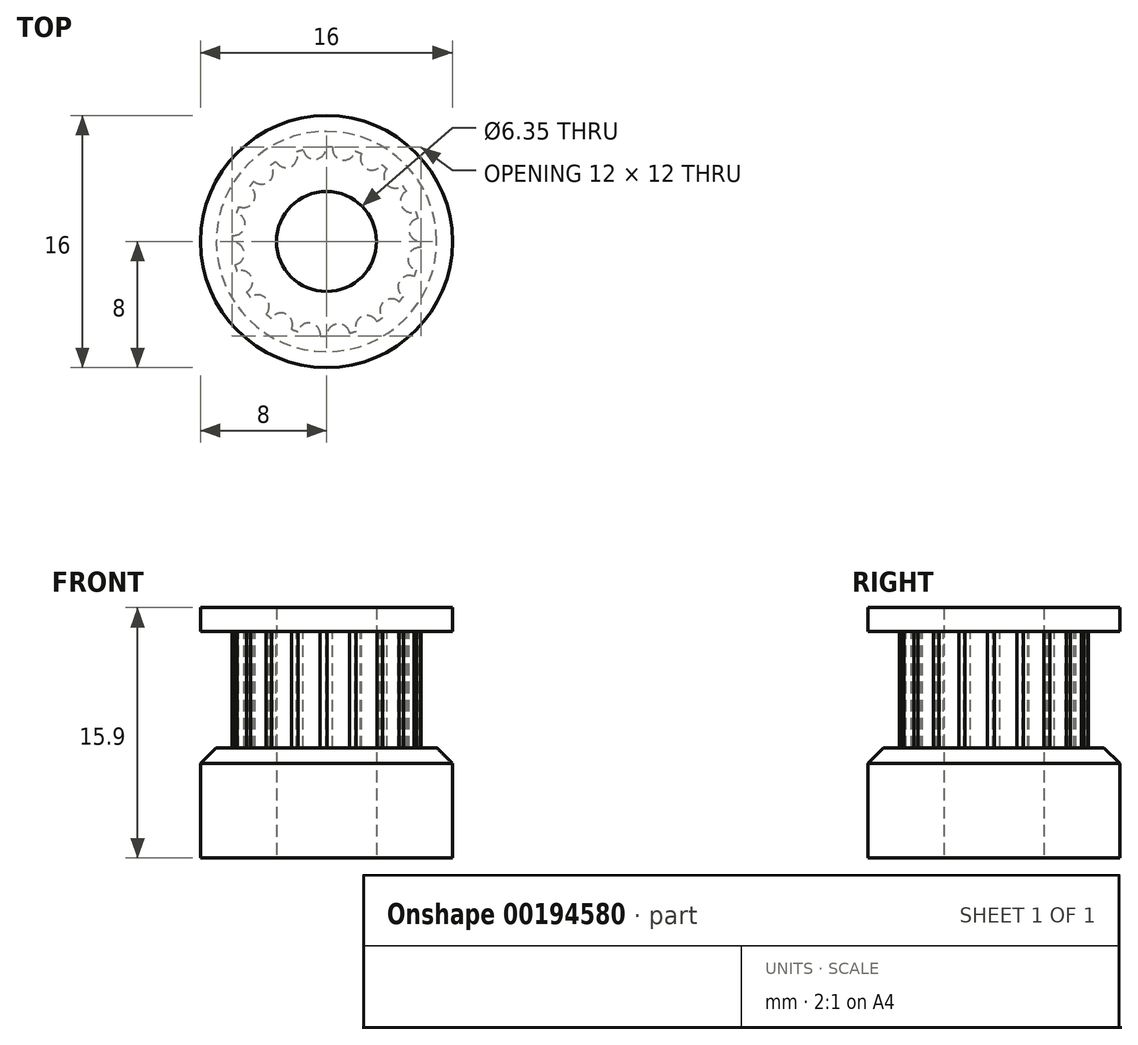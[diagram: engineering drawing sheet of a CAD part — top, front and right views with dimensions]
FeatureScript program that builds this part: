
annotation { "Feature Type Name" : "Feature", "Feature Type Description" : "" }
export const myFeature = defineFeature(function(context is Context, id is Id, definition is map)
    precondition{}
    {
        {
            var Q0;
            Q0=qCreatedBy(makeId("Top.planeOp"),FACE);
            var sketch = newSketch(context, id + "F0", { "sketchPlane" : qUnion([Q0])});
            skCircle(sketch, "E0", {"center": v(0, 0) * mm, "radius": 8 * mm});
            skSolve(sketch);
        }
        {
            var Q0;
            Q0 = qSketchRegion(id + "F0", true);
            extrude(context, id + "F1", {"entities" : qUnion([Q0]), "depth" : 7 * mm});
        }
        {
            var Q0;
            Q0=makeQuery(id+"F1.opExtrude","CAP_FACE",FACE,{"disambiguationData":[OSD([sQuery(id+"F0.wireOp",EDGE,"E0")])],"isStart":false});
            var sketch = newSketch(context, id + "F2", { "sketchPlane" : qUnion([Q0])});
            skCircle(sketch, "E1", {"center": v(0, 0) * mm, "radius": 6 * mm});
            skSolve(sketch);
        }
        {
            var Q0;
            Q0 = qSketchRegion(id + "F2", true);
            extrude(context, id + "F3", {"entities" : qUnion([Q0]), "operationType" : NewBodyOperationType.ADD, "depth" : 7.4 * mm});
        }
        {
            var Q0;
            Q0=makeQuery(id+"F1.opExtrude","CAP_EDGE",EDGE,{"disambiguationData":[OSD([sQuery(id+"F0.wireOp",EDGE,"E0")])],"isStart":false});
            chamfer(context, id + "F4", {"entities" : qUnion([Q0]), "width" : 1 * mm, "tangentPropagation" : true});
        }
        {
            var Q0;
            Q0=makeQuery(id+"F3.opExtrude","CAP_FACE",FACE,{"disambiguationData":[OSD([sQuery(id+"F2.wireOp",EDGE,"E1")])],"isStart":false});
            var sketch = newSketch(context, id + "F5", { "sketchPlane" : qUnion([Q0])});
            skCircle(sketch, "E2", {"center": v(0, 0) * mm, "radius": 8 * mm});
            skSolve(sketch);
        }
        {
            var Q0;
            Q0 = qSketchRegion(id + "F5", true);
            extrude(context, id + "F6", {"entities" : qUnion([Q0]), "operationType" : NewBodyOperationType.ADD, "depth" : 1.5 * mm});
        }
        {
            var Q0;
            Q0=makeQuery(id+"F6.opExtrude","CAP_FACE",FACE,{"disambiguationData":[OSD([sQuery(id+"F5.wireOp",EDGE,"E2")])],"isStart":true});
            var sketch = newSketch(context, id + "F7", { "sketchPlane" : qUnion([Q0])});
            skCircle(sketch, "E3", {"center": v(-5.42, 2.56) * mm, "radius": 0.72 * mm});
            skCircle(sketch, "E4.1.0", {"center": v(-5.95, 0.76) * mm, "radius": 0.72 * mm});
            skCircle(sketch, "E4.2.0", {"center": v(-5.9, -1.11) * mm, "radius": 0.72 * mm});
            skCircle(sketch, "E4.3.0", {"center": v(-5.26, -2.88) * mm, "radius": 0.72 * mm});
            skCircle(sketch, "E4.4.0", {"center": v(-4.12, -4.37) * mm, "radius": 0.72 * mm});
            skCircle(sketch, "E4.5.0", {"center": v(-2.56, -5.42) * mm, "radius": 0.72 * mm});
            skCircle(sketch, "E4.6.0", {"center": v(-0.76, -5.95) * mm, "radius": 0.72 * mm});
            skCircle(sketch, "E4.7.0", {"center": v(1.11, -5.9) * mm, "radius": 0.72 * mm});
            skCircle(sketch, "E4.8.0", {"center": v(2.88, -5.26) * mm, "radius": 0.72 * mm});
            skCircle(sketch, "E4.9.0", {"center": v(4.37, -4.12) * mm, "radius": 0.72 * mm});
            skCircle(sketch, "E4.10.0", {"center": v(5.42, -2.56) * mm, "radius": 0.72 * mm});
            skCircle(sketch, "E4.11.0", {"center": v(5.95, -0.76) * mm, "radius": 0.72 * mm});
            skCircle(sketch, "E4.12.0", {"center": v(5.9, 1.11) * mm, "radius": 0.72 * mm});
            skCircle(sketch, "E4.13.0", {"center": v(5.26, 2.88) * mm, "radius": 0.72 * mm});
            skCircle(sketch, "E4.14.0", {"center": v(4.12, 4.37) * mm, "radius": 0.72 * mm});
            skCircle(sketch, "E4.15.0", {"center": v(2.56, 5.42) * mm, "radius": 0.72 * mm});
            skCircle(sketch, "E4.16.0", {"center": v(0.76, 5.95) * mm, "radius": 0.72 * mm});
            skCircle(sketch, "E4.17.0", {"center": v(-1.11, 5.9) * mm, "radius": 0.72 * mm});
            skCircle(sketch, "E4.18.0", {"center": v(-2.88, 5.26) * mm, "radius": 0.72 * mm});
            skCircle(sketch, "E4.19.0", {"center": v(-4.37, 4.12) * mm, "radius": 0.72 * mm});
            skPoint(sketch, "E4.center", {"position": v(0, 0) * mm});
            skSolve(sketch);
        }
        {
            var Q0;
            Q0 = qSketchRegion(id + "F7", true);
            extrude(context, id + "F8", {"entities" : qUnion([Q0]), "operationType" : NewBodyOperationType.REMOVE, "depth" : 7.4 * mm});
        }
        {
            var Q0;
            Q0=makeQuery(id+"F6.opExtrude","CAP_FACE",FACE,{"disambiguationData":[OSD([sQuery(id+"F5.wireOp",EDGE,"E2")])],"isStart":false});
            var sketch = newSketch(context, id + "F9", { "sketchPlane" : qUnion([Q0])});
            skPoint(sketch, "E5", {"position": v(0, 0) * mm});
            skSolve(sketch);
        }
        {
            var Q0;
            Q0=sQuery(id+"F9.wireOp",VERTEX,"E5");
            var Q1;
            Q1=makeQuery(id+"F1.opExtrude","SWEPT_BODY",BODY,{"disambiguationData":[OSD([sQuery(id+"F0.wireOp",EDGE,"E0")])]});
            hole(context, id + "F10", {"style" : HoleStyle.SIMPLE, "endStyle" : HoleEndStyle.THROUGH, "holeDiameter" : 6.35 * mm, "locations" : qUnion([Q0]), "scope" : qUnion([Q1]), "isTappedThrough" : true, "startStyle" : HoleStartStyle.PART});
        }
    });
